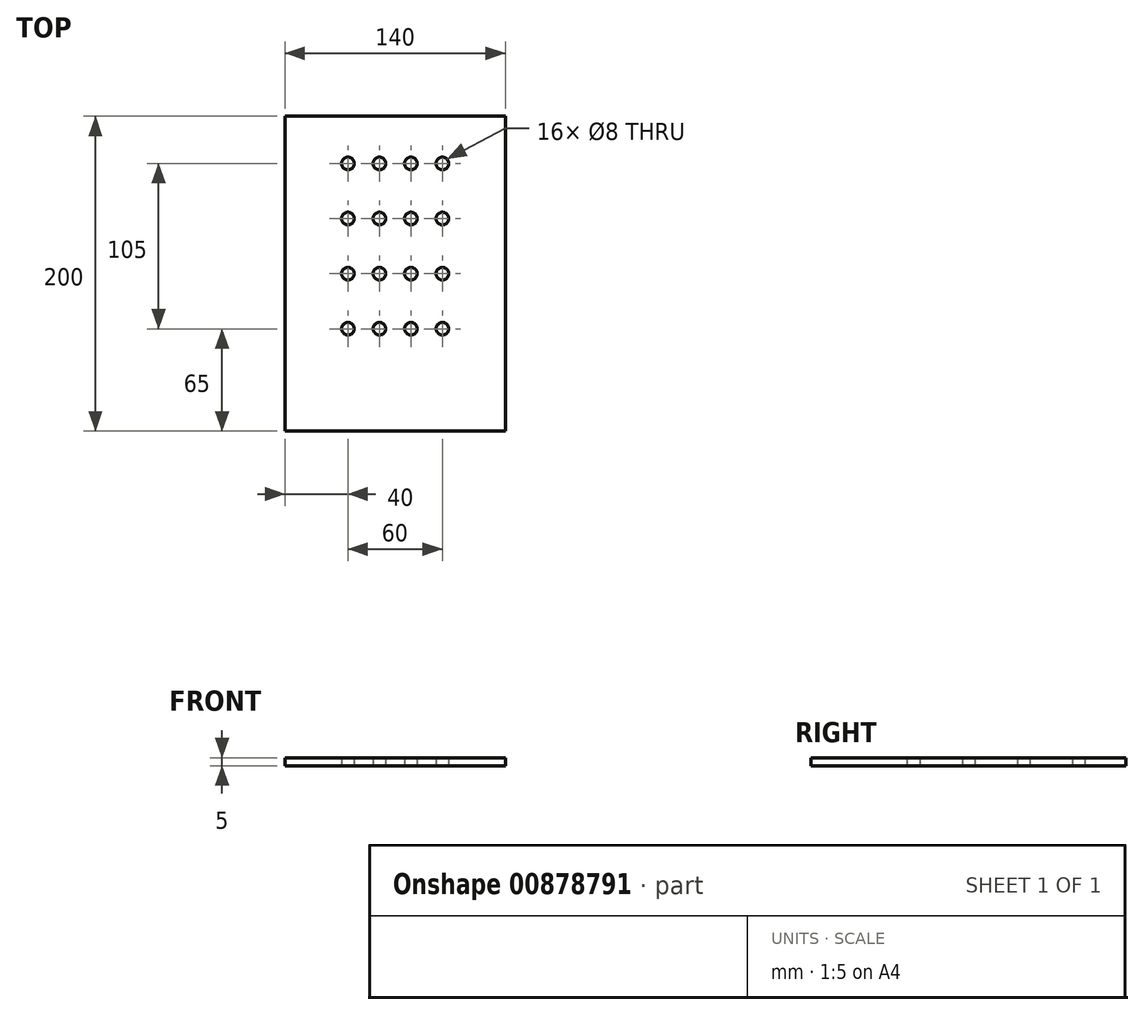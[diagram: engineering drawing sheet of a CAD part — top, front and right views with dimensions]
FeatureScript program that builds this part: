
annotation { "Feature Type Name" : "Feature", "Feature Type Description" : "" }
export const myFeature = defineFeature(function(context is Context, id is Id, definition is map)
    precondition{}
    {
        {
            var Q0;
            Q0=qCreatedBy(makeId("Top.planeOp"),FACE);
            var sketch = newSketch(context, id + "F0", { "sketchPlane" : qUnion([Q0])});
            skLineSegment(sketch, "E0.bottom", {"start": v(-70, 100) * mm, "end": v(70, 100) * mm});
            skLineSegment(sketch, "E0.top", {"start": v(-70, -100) * mm, "end": v(70, -100) * mm});
            skLineSegment(sketch, "E0.left", {"start": v(-70, 100) * mm, "end": v(-70, -100) * mm});
            skLineSegment(sketch, "E0.right", {"start": v(70, 100) * mm, "end": v(70, -100) * mm});
            skLineSegment(sketch, "E1.MirrorCS", {"start": v(-210, 100) * mm, "end": v(-210, -100) * mm});
            skCircle(sketch, "E2", {"center": v(-30, 70) * mm, "radius": 4 * mm});
            skCircle(sketch, "E3.0.1.0", {"center": v(-30, 35) * mm, "radius": 4 * mm});
            skCircle(sketch, "E3.0.2.0", {"center": v(-30, 0) * mm, "radius": 4 * mm});
            skCircle(sketch, "E3.0.3.0", {"center": v(-30, -35) * mm, "radius": 4 * mm});
            skCircle(sketch, "E3.1.0.0", {"center": v(-10, 70) * mm, "radius": 4 * mm});
            skCircle(sketch, "E3.1.1.0", {"center": v(-10, 35) * mm, "radius": 4 * mm});
            skCircle(sketch, "E3.1.2.0", {"center": v(-10, 0) * mm, "radius": 4 * mm});
            skCircle(sketch, "E3.1.3.0", {"center": v(-10, -35) * mm, "radius": 4 * mm});
            skCircle(sketch, "E3.2.0.0", {"center": v(10, 70) * mm, "radius": 4 * mm});
            skCircle(sketch, "E3.2.1.0", {"center": v(10, 35) * mm, "radius": 4 * mm});
            skCircle(sketch, "E3.2.2.0", {"center": v(10, 0) * mm, "radius": 4 * mm});
            skCircle(sketch, "E3.2.3.0", {"center": v(10, -35) * mm, "radius": 4 * mm});
            skCircle(sketch, "E3.3.0.0", {"center": v(30, 70) * mm, "radius": 4 * mm});
            skCircle(sketch, "E3.3.1.0", {"center": v(30, 35) * mm, "radius": 4 * mm});
            skCircle(sketch, "E3.3.2.0", {"center": v(30, 0) * mm, "radius": 4 * mm});
            skCircle(sketch, "E3.3.3.0", {"center": v(30, -35) * mm, "radius": 4 * mm});
            skLineSegment(sketch, "E3.direction1", {"start": v(-30, 55) * mm, "end": v(-10, 55) * mm, "construction": true});
            skLineSegment(sketch, "E3.direction2", {"start": v(-30, 55) * mm, "end": v(-30, 35) * mm, "construction": true});
            skSolve(sketch);
        }
        {
            var Q0;
            Q0=makeQuery(id+"F0.imprint","IMPRINT",FACE,{"disambiguationData":[TD([[makeQuery(id+"F0.imprint","IMPRINT",EDGE,{"derivedFrom":sQuery(id+"F0.wireOp",EDGE,"E0.bottom")}),-1.0]])]});
            extrude(context, id + "F1", {"entities" : qUnion([Q0]), "depth" : 5 * mm, "offsetDistance" : 25 * mm});
        }
    });
